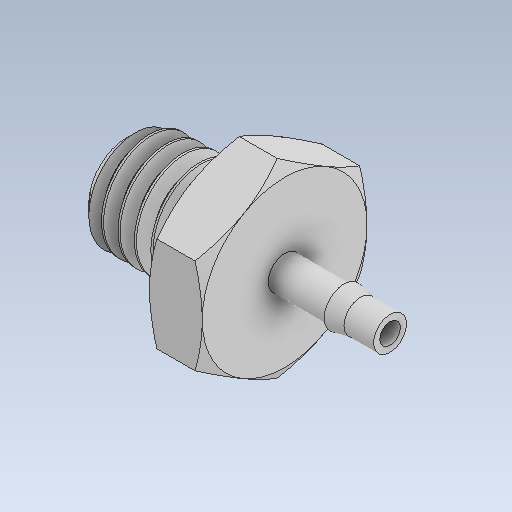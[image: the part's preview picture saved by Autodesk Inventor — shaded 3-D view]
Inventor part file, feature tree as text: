
AUTODESK INVENTOR PART (.ipt)
format: ipt  version: 2021.2 (Build 252289000, 289)  size: 518,656 bytes
history: native  units: in
note: dims shown in document units (in); Inventor stores cm internally (conversion verified against a paired STEP export)
features: chamfer x1
ambient origin geometry x8: Origin, YZ Plane, XZ Plane, XY Plane, X Axis, Y Axis, Z Axis, Center Point
bodies: Solid1 (feature_tree)
feature tree (1):
  chamfer  "Chamfer1"  [1 undecoded]
note: 1 required parameter value undecoded (feature->parameter linkage not recoverable at this tier; creation-order binding heuristic only, values carry confidence <= 0.55)
